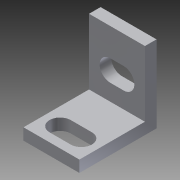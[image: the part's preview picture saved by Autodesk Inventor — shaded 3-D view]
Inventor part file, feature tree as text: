
AUTODESK INVENTOR PART (.ipt)
format: ipt  version: 2014 SP1 (Build 180222100, 222)  size: 116,224 bytes
history: native  units: in
note: dims shown in document units (in); Inventor stores cm internally (conversion verified against a paired STEP export)
features: extrude x3, sketch x3, plane x1
ambient origin geometry x8: Origin, YZ Plane, XZ Plane, XY Plane, X Axis, Y Axis, Z Axis, Center Point
bodies: Solid1 (feature_tree)
feature tree (7):
  extrude  "Extrusion1"  Depth=0.5709in
  extrude  "Extrusion2"  Depth=0.2165in
  extrude  "Extrusion3"  Depth=0.1181in TaperAngle=0.0deg
  plane  "Work Plane2"
  sketch  "Sketch1"  dims[d0=0.7874in d1=0.5709in]
  sketch  "Sketch2"  dims[d2=0.2165in d3=0.1378in]
  sketch  "Sketch3"  dims[d4=0.3937in d5=0.1181in d6=0.0in d7=0.1181in d8=0.6693in d9=0.0in d10=0.2165in d11=0.2165in d12=0.1969in d13=0.6693in d14=0.0in]
